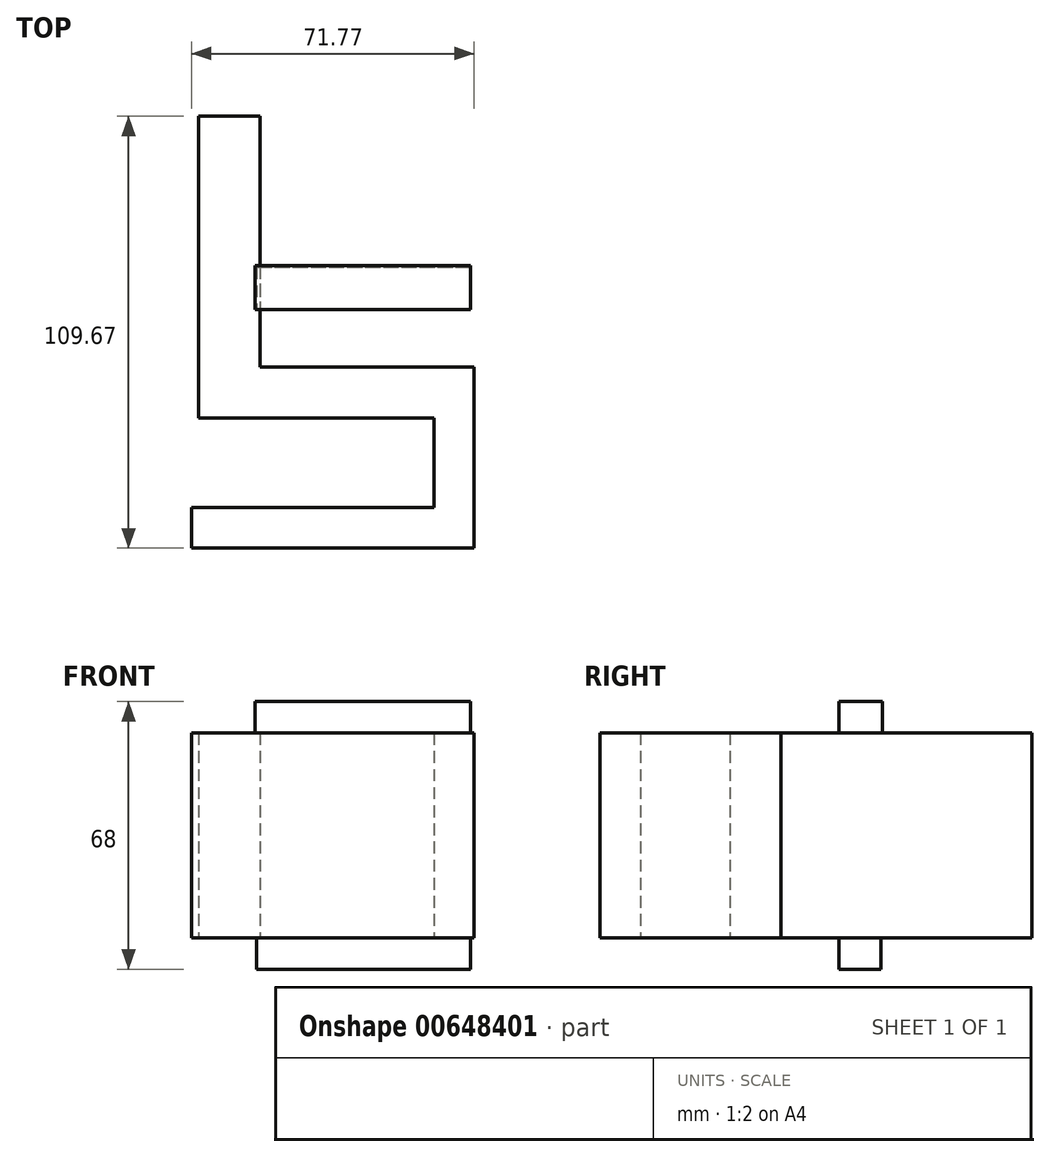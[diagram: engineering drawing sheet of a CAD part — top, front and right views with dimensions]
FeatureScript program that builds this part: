
annotation { "Feature Type Name" : "Feature", "Feature Type Description" : "" }
export const myFeature = defineFeature(function(context is Context, id is Id, definition is map)
    precondition{}
    {
        {
            var Q0;
            Q0=qCreatedBy(makeId("Top.planeOp"),FACE);
            var sketch = newSketch(context, id + "F0", { "sketchPlane" : qUnion([Q0])});
            skLineSegment(sketch, "E0", {"start": v(-47.48, 43.91) * mm, "end": v(-31.88, 43.91) * mm});
            skLineSegment(sketch, "E1", {"start": v(-31.88, 43.91) * mm, "end": v(-31.88, -19.84) * mm});
            skLineSegment(sketch, "E2", {"start": v(-31.88, -19.84) * mm, "end": v(22.51, -19.84) * mm});
            skLineSegment(sketch, "E3", {"start": v(22.51, -19.84) * mm, "end": v(22.51, -32.77) * mm});
            skLineSegment(sketch, "E4", {"start": v(22.51, -32.77) * mm, "end": v(22.51, -65.76) * mm});
            skLineSegment(sketch, "E5", {"start": v(22.51, -65.76) * mm, "end": v(-43.47, -65.76) * mm});
            skLineSegment(sketch, "E6", {"start": v(-43.02, -32.77) * mm, "end": v(-47.48, -32.77) * mm});
            skLineSegment(sketch, "E7", {"start": v(-43.47, -65.76) * mm, "end": v(-49.26, -65.76) * mm});
            skLineSegment(sketch, "E8", {"start": v(-49.26, -65.76) * mm, "end": v(-49.26, -55.5) * mm});
            skLineSegment(sketch, "E9", {"start": v(-49.26, -55.5) * mm, "end": v(12.26, -55.5) * mm});
            skLineSegment(sketch, "E10", {"start": v(12.26, -55.5) * mm, "end": v(12.26, -32.77) * mm});
            skLineSegment(sketch, "E11", {"start": v(12.26, -32.77) * mm, "end": v(-47.48, -32.77) * mm});
            skLineSegment(sketch, "E12", {"start": v(-47.48, 43.91) * mm, "end": v(-47.48, -32.77) * mm});
            skSolve(sketch);
        }
        {
            var Q0;
            Q0 = qSketchRegion(id + "F0", true);
            extrude(context, id + "F1", {"entities" : qUnion([Q0]), "depth" : 52 * mm, "offsetDistance" : 25.4 * mm});
        }
        {
            var Q0;
            Q0=qCreatedBy(makeId("Top.planeOp"),FACE);
            cPlane(context, id + "F2", {"entities" : qUnion([Q0]), "cplaneType" : CPlaneType.OFFSET, "offset" : 52 * mm, "width" : 150 * mm, "height" : 150 * mm});
        }
        {
            var Q0;
            Q0=qCreatedBy(makeId("Top.planeOp"),FACE);
            var sketch = newSketch(context, id + "F3", { "sketchPlane" : qUnion([Q0])});
            skLineSegment(sketch, "E13.bottom", {"start": v(-32.77, 5.57) * mm, "end": v(21.62, 5.57) * mm});
            skLineSegment(sketch, "E13.top", {"start": v(-32.77, -5.13) * mm, "end": v(21.62, -5.13) * mm});
            skLineSegment(sketch, "E13.left", {"start": v(-32.77, 5.57) * mm, "end": v(-32.77, -5.13) * mm});
            skLineSegment(sketch, "E13.right", {"start": v(21.62, 5.57) * mm, "end": v(21.62, -5.13) * mm});
            skSolve(sketch);
        }
        {
            var Q0;
            Q0 = qSketchRegion(id + "F3", true);
            extrude(context, id + "F4", {"entities" : qUnion([Q0]), "operationType" : NewBodyOperationType.ADD, "oppositeDirection" : true, "depth" : 8 * mm, "offsetDistance" : 25 * mm});
        }
        {
            var Q0;
            Q0=qCreatedBy(id+"F2.planeOp",FACE);
            var sketch = newSketch(context, id + "F5", { "sketchPlane" : qUnion([Q0])});
            skLineSegment(sketch, "E14.bottom", {"start": v(21.62, 6.02) * mm, "end": v(-33.21, 6.02) * mm});
            skLineSegment(sketch, "E14.top", {"start": v(21.62, -5.13) * mm, "end": v(-33.21, -5.13) * mm});
            skLineSegment(sketch, "E14.left", {"start": v(21.62, 6.02) * mm, "end": v(21.62, -5.13) * mm});
            skLineSegment(sketch, "E14.right", {"start": v(-33.21, 6.02) * mm, "end": v(-33.21, -5.13) * mm});
            skSolve(sketch);
        }
        {
            var Q0;
            Q0 = qSketchRegion(id + "F5", true);
            extrude(context, id + "F6", {"entities" : qUnion([Q0]), "operationType" : NewBodyOperationType.ADD, "depth" : 8 * mm, "offsetDistance" : 25 * mm});
        }
    });
